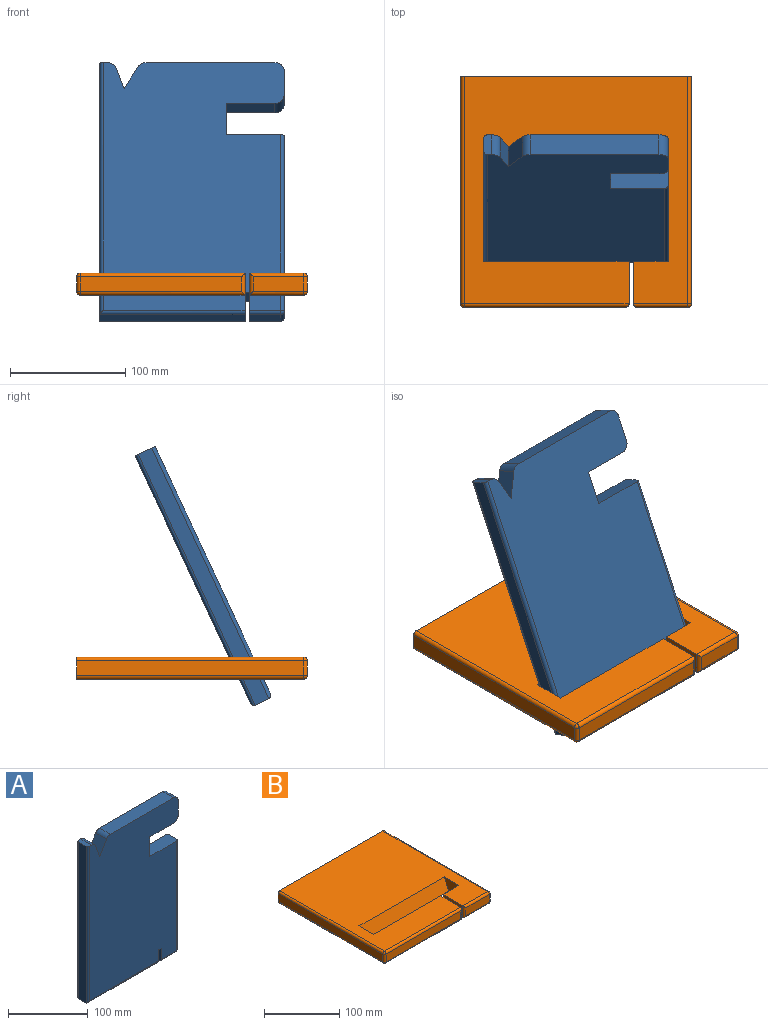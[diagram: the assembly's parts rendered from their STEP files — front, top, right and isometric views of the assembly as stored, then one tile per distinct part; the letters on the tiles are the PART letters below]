
ASSEMBLY  parts=2 mates=1
PART A: 32 faces, bbox 160x19x240 mm
  f0: plane 23x19mm, normal (1,0,0), area 437mm2, adj f7,f8,f28,f31
  f1: plane 111.87x19mm, normal (0,0,1), area 2125.5mm2, adj f7,f8,f29,f31
  f2: plane 27x13mm, normal (0,0,-1), area 351mm2, adj f9,f19,f22,f23
  f3: plane 168x13mm, normal (1,0,0), area 2184mm2, adj f13,f20,f23,f25
  f4: plane 19x6.76mm, normal (0,0,1), area 124.6mm2, adj f5,f7,f8,f17,f26,f30
  f5: plane 240x13mm, normal (-1,0,0), area 3120mm2, adj f4,f6,f17,f26
  f6: plane 126x13mm, normal (0,0,-1), area 1638mm2, adj f5,f10,f18,f27
  f7: plane 237x157mm, normal (0,1,0), area 34815.9mm2, adj f0,f1,f4,f9,f10,f11,f12,f13
  f8: plane 237x157mm, normal (0,-1,0), area 34815.9mm2, adj f0,f1,f4,f9,f10,f11,f12,f13
  f9: plane 20x19mm, normal (-1,0,0), area 376.1mm2, adj f2,f7,f8,f11,f19,f22
  f10: plane 20x19mm, normal (1,0,0), area 376.1mm2, adj f6,f7,f8,f11,f18,f27
  f11: plane 19x4mm, normal (0,0,-1), area 76mm2, adj f7,f8,f9,f10
  f12: plane 42x19mm, normal (0,0,-1), area 798mm2, adj f7,f8,f14,f28
  f13: plane 50x19mm, normal (0,0,1), area 946.1mm2, adj f3,f7,f8,f14,f20,f25
  f14: plane 30x19mm, normal (1,0,0), area 570mm2, adj f7,f8,f12,f13
  f15: plane 19.26x19mm, normal (0.94,0,0.33), area 388.2mm2, adj f7,f8,f16,f30
  f16: plane 20.64x19mm, normal (-0.86,0,0.51), area 454.6mm2, adj f7,f8,f15,f29
  f17: cylinder r=3mm len=240mm, axis (0,0,1), area 1125.8mm2, adj f4,f5,f7,f18
  f18: cylinder r=3mm len=126mm, axis (-1,0,0), area 588.6mm2, adj f6,f7,f10,f17
  f19: cylinder r=3mm len=27mm, axis (1,0,0), area 127.2mm2, adj f2,f8,f9,f21
  f20: cylinder r=3mm len=168mm, axis (0,0,1), area 791.7mm2, adj f3,f8,f13,f21
  f21: sphere r=3mm, area 14.1mm2, adj f19,f20,f23
  f22: cylinder r=3mm len=27mm, axis (-1,0,0), area 127.2mm2, adj f2,f7,f9,f24
  f23: cylinder r=3mm len=13mm, axis (0,-1,0), area 61.3mm2, adj f2,f3,f21,f24
  f24: sphere r=3mm, area 14.1mm2, adj f22,f23,f25
  f25: cylinder r=3mm len=168mm, axis (0,0,-1), area 791.7mm2, adj f3,f7,f13,f24
  f26: cylinder r=3mm len=240mm, axis (0,0,-1), area 1125.8mm2, adj f4,f5,f8,f27
  f27: cylinder r=3mm len=126mm, axis (1,0,0), area 588.6mm2, adj f6,f8,f10,f26
  f28: cylinder r=8mm len=19mm, axis (0,-1,0), area 238.8mm2, adj f0,f7,f8,f12
  f29: cylinder r=8mm len=19mm, axis (0,1,0), area 158.1mm2, adj f1,f7,f8,f16
  f30: cylinder r=8mm len=19mm, axis (0,1,0), area 187mm2, adj f4,f7,f8,f15
  f31: cylinder r=8mm len=19mm, axis (0,1,0), area 238.8mm2, adj f0,f1,f7,f8
PART B: 30 faces, bbox 200x200x19 mm
  f0: plane 197x194mm, normal (0,0,-1), area 35030mm2, adj f3,f5,f8,f9,f10,f11,f12,f13
  f1: plane 197x194mm, normal (0,0,1), area 33612.4mm2, adj f3,f5,f8,f9,f10,f11,f12,f13
  f2: plane 44x13mm, normal (0,-1,0), area 572mm2, adj f24,f27,f28,f29
  f3: plane 30x19mm, normal (0,1,0), area 570mm2, adj f0,f1,f8,f13
  f4: plane 197x13mm, normal (1,0,0), area 2561mm2, adj f5,f22,f23,f24
  f5: plane 200x19mm, normal (0,1,0), area 3792.3mm2, adj f0,f1,f4,f6,f14,f17,f22,f23
  f6: plane 197x13mm, normal (-1,0,0), area 2561mm2, adj f5,f14,f17,f18
  f7: plane 140x13mm, normal (0,-1,0), area 1820mm2, adj f16,f18,f19,f21
  f8: plane 27.86x19mm, normal (-1,0,0), area 445.2mm2, adj f0,f1,f3,f11
  f9: plane 27.86x19mm, normal (1,0,0), area 445.2mm2, adj f0,f1,f10,f11
  f10: plane 126x19mm, normal (0,1,0), area 2394mm2, adj f0,f1,f9,f12
  f11: plane 160x19mm, normal (0,-0.91,0.42), area 3354.3mm2, adj f0,f1,f8,f9
  f12: plane 37x19mm, normal (1,0,0), area 703mm2, adj f0,f1,f10,f19
  f13: plane 37x19mm, normal (-1,0,0), area 703mm2, adj f0,f1,f3,f29
  f14: cylinder r=3mm len=197mm, axis (0,-1,0), area 928.3mm2, adj f1,f5,f6,f15
  f15: sphere r=3mm, area 14.1mm2, adj f14,f16,f18
  f16: cylinder r=3mm len=143mm, axis (1,0,0), area 668.7mm2, adj f1,f7,f15,f19
  f17: cylinder r=3mm len=197mm, axis (0,1,0), area 928.3mm2, adj f0,f5,f6,f20
  f18: cylinder r=3mm len=13mm, axis (0,0,-1), area 61.3mm2, adj f6,f7,f15,f20
  f19: cylinder r=3mm len=19mm, axis (0,0,-1), area 79.3mm2, adj f7,f12,f16,f21
  f20: sphere r=3mm, area 14.1mm2, adj f17,f18,f21
  f21: cylinder r=3mm len=143mm, axis (-1,0,0), area 668.7mm2, adj f0,f7,f19,f20
  f22: cylinder r=3mm len=197mm, axis (0,-1,0), area 928.3mm2, adj f0,f4,f5,f25
  f23: cylinder r=3mm len=197mm, axis (0,1,0), area 928.3mm2, adj f1,f4,f5,f26
  f24: cylinder r=3mm len=13mm, axis (0,0,1), area 61.3mm2, adj f2,f4,f25,f26
  f25: sphere r=3mm, area 14.1mm2, adj f22,f24,f27
  f26: sphere r=3mm, area 14.1mm2, adj f23,f24,f28
  f27: cylinder r=3mm len=47mm, axis (-1,0,0), area 216.3mm2, adj f0,f2,f25,f29
  f28: cylinder r=3mm len=47mm, axis (1,0,0), area 216.3mm2, adj f1,f2,f26,f29
  f29: cylinder r=3mm len=19mm, axis (0,0,1), area 79.3mm2, adj f2,f13,f27,f28
PLACE A rot(axis=(-1,0,0),25deg) t=(-0.27,-18.79,83.42)mm
PLACE B t=(-0.27,-0.15,9.51)mm
MATE planar A.f7 <-> B.f11  axis (0,0.91,-0.42) through (-1.84,-2.23,73.96)mm
